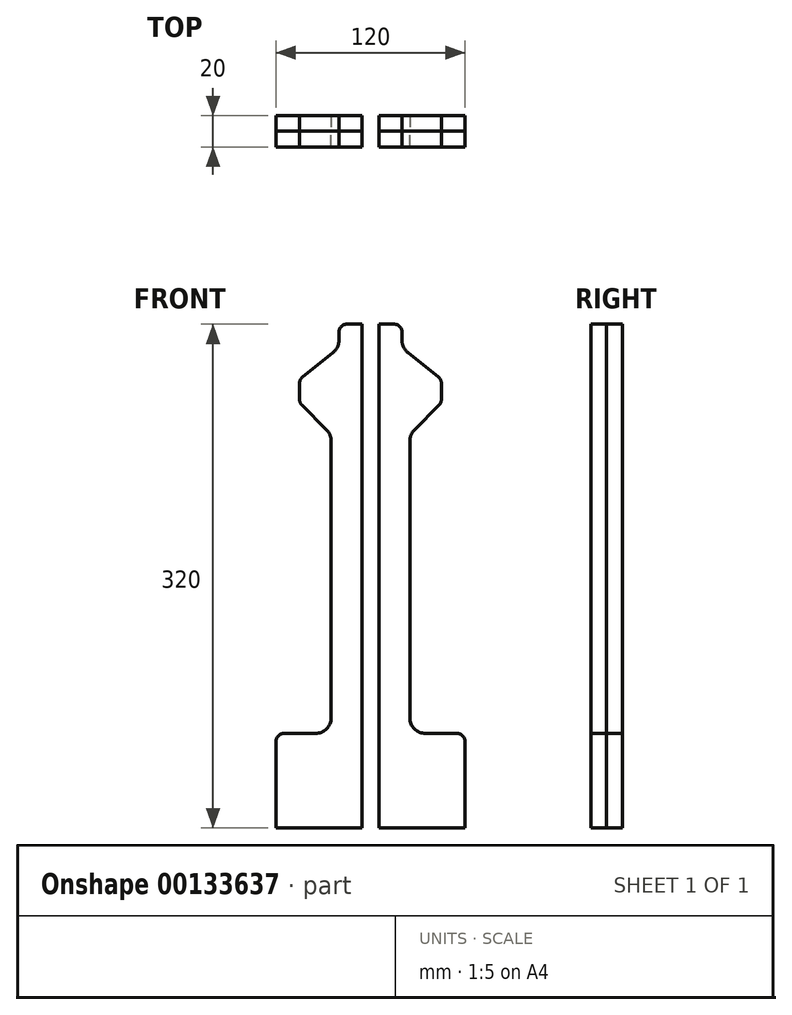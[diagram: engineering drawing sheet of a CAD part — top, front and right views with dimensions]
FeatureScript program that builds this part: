
annotation { "Feature Type Name" : "Feature", "Feature Type Description" : "" }
export const myFeature = defineFeature(function(context is Context, id is Id, definition is map)
    precondition{}
    {
        {
            var Q0;
            Q0=qCreatedBy(makeId("Front.planeOp"),FACE);
            var sketch = newSketch(context, id + "F0", { "sketchPlane" : qUnion([Q0])});
            skLineSegment(sketch, "E0.bottom", {"start": v(55, 30) * mm, "end": v(35, 30) * mm});
            skLineSegment(sketch, "E0.top", {"start": v(60, -30) * mm, "end": v(-60, -30) * mm});
            skLineSegment(sketch, "E0.left", {"start": v(60, 25) * mm, "end": v(60, -30) * mm});
            skLineSegment(sketch, "E0.right", {"start": v(-60, 25) * mm, "end": v(-60, -30) * mm});
            skPoint(sketch, "E0.middle", {"position": v(0, 0) * mm});
            skLineSegment(sketch, "E1", {"start": v(25, 40) * mm, "end": v(25, 215.86) * mm});
            skLineSegment(sketch, "E2", {"start": v(27.93, 222.93) * mm, "end": v(43.54, 238.54) * mm});
            skLineSegment(sketch, "E3", {"start": v(45, 242.07) * mm, "end": v(45, 252.6) * mm});
            skLineSegment(sketch, "E4", {"start": v(43.12, 256.5) * mm, "end": v(23.75, 272) * mm});
            skLineSegment(sketch, "E5", {"start": v(20, 279.8) * mm, "end": v(20, 285) * mm});
            skLineSegment(sketch, "E6", {"start": v(15, 290) * mm, "end": v(-15, 290) * mm});
            skLineSegment(sketch, "E7", {"start": v(-20, 285) * mm, "end": v(-20, 279.8) * mm});
            skLineSegment(sketch, "E8", {"start": v(-23.75, 272) * mm, "end": v(-43.12, 256.5) * mm});
            skLineSegment(sketch, "E9", {"start": v(-45, 252.6) * mm, "end": v(-45, 242.07) * mm});
            skLineSegment(sketch, "E10", {"start": v(-43.54, 238.54) * mm, "end": v(-27.93, 222.93) * mm});
            skLineSegment(sketch, "E11", {"start": v(-25, 215.86) * mm, "end": v(-25, 40) * mm});
            skPoint(sketch, "E12.visualSharp", {"position": v(25, 220) * mm});
            skArc(sketch, "E12.filletArc", {"start": v(27.93, 222.93) * mm, "mid": v(25.76, 219.68) * mm, "end": v(25, 215.86) * mm});
            skPoint(sketch, "E13.visualSharp", {"position": v(-25, 220) * mm});
            skArc(sketch, "E13.filletArc", {"start": v(-25, 215.86) * mm, "mid": v(-25.76, 219.68) * mm, "end": v(-27.93, 222.93) * mm});
            skPoint(sketch, "E14.visualSharp", {"position": v(-20, 275) * mm});
            skArc(sketch, "E14.filletArc", {"start": v(-23.75, 272) * mm, "mid": v(-20.99, 275.47) * mm, "end": v(-20, 279.8) * mm});
            skPoint(sketch, "E15.visualSharp", {"position": v(20, 275) * mm});
            skArc(sketch, "E15.filletArc", {"start": v(20, 279.8) * mm, "mid": v(20.99, 275.47) * mm, "end": v(23.75, 272) * mm});
            skPoint(sketch, "E16.visualSharp", {"position": v(-20, 290) * mm});
            skArc(sketch, "E16.filletArc", {"start": v(-15, 290) * mm, "mid": v(-18.54, 288.54) * mm, "end": v(-20, 285) * mm});
            skPoint(sketch, "E17.visualSharp", {"position": v(20, 290) * mm});
            skArc(sketch, "E17.filletArc", {"start": v(20, 285) * mm, "mid": v(18.54, 288.54) * mm, "end": v(15, 290) * mm});
            skPoint(sketch, "E18.visualSharp", {"position": v(45, 255) * mm});
            skArc(sketch, "E18.filletArc", {"start": v(45, 252.6) * mm, "mid": v(44.5, 254.76) * mm, "end": v(43.12, 256.5) * mm});
            skPoint(sketch, "E19.visualSharp", {"position": v(45, 240) * mm});
            skArc(sketch, "E19.filletArc", {"start": v(43.54, 238.54) * mm, "mid": v(44.62, 240.16) * mm, "end": v(45, 242.07) * mm});
            skPoint(sketch, "E20.visualSharp", {"position": v(-45, 240) * mm});
            skArc(sketch, "E20.filletArc", {"start": v(-45, 242.07) * mm, "mid": v(-44.62, 240.16) * mm, "end": v(-43.54, 238.54) * mm});
            skPoint(sketch, "E21.visualSharp", {"position": v(-45, 255) * mm});
            skArc(sketch, "E21.filletArc", {"start": v(-43.12, 256.5) * mm, "mid": v(-44.5, 254.76) * mm, "end": v(-45, 252.6) * mm});
            skLineSegment(sketch, "E22", {"start": v(-55, 30) * mm, "end": v(-35, 30) * mm});
            skLineSegment(sketch, "E23", {"start": v(25, 30) * mm, "end": v(60, 30) * mm});
            skPoint(sketch, "E24.newPointA", {"position": v(25, 30) * mm});
            skPoint(sketch, "E24.newPointB", {"position": v(-60, 30) * mm});
            skArc(sketch, "E24.filletArc", {"start": v(25, 40) * mm, "mid": v(27.93, 32.93) * mm, "end": v(35, 30) * mm});
            skPoint(sketch, "E25.visualSharp", {"position": v(-25, 30) * mm});
            skArc(sketch, "E25.filletArc", {"start": v(-35, 30) * mm, "mid": v(-27.93, 32.93) * mm, "end": v(-25, 40) * mm});
            skArc(sketch, "E26.filletArc", {"start": v(-55, 30) * mm, "mid": v(-58.54, 28.54) * mm, "end": v(-60, 25) * mm});
            skPoint(sketch, "E27.visualSharp", {"position": v(60, 30) * mm});
            skArc(sketch, "E27.filletArc", {"start": v(60, 25) * mm, "mid": v(58.54, 28.54) * mm, "end": v(55, 30) * mm});
            skLineSegment(sketch, "E28.bottom", {"start": v(-5.5, 290) * mm, "end": v(5.5, 290) * mm});
            skLineSegment(sketch, "E28.top", {"start": v(-5.5, 130) * mm, "end": v(5.5, 130) * mm});
            skLineSegment(sketch, "E28.left", {"start": v(-5.5, 290) * mm, "end": v(-5.5, 130) * mm});
            skLineSegment(sketch, "E28.right", {"start": v(5.5, 290) * mm, "end": v(5.5, 130) * mm});
            skPoint(sketch, "E28.middle", {"position": v(0, 210) * mm});
            skLineSegment(sketch, "E29.bottom", {"start": v(5.5, 130) * mm, "end": v(-5.5, 130) * mm});
            skLineSegment(sketch, "E29.top", {"start": v(5.5, -30) * mm, "end": v(-5.5, -30) * mm});
            skLineSegment(sketch, "E29.left", {"start": v(5.5, 130) * mm, "end": v(5.5, -30) * mm});
            skLineSegment(sketch, "E29.right", {"start": v(-5.5, 130) * mm, "end": v(-5.5, -30) * mm});
            skPoint(sketch, "E29.middle", {"position": v(0, 50) * mm});
            skSolve(sketch);
        }
        {
            var Q0;
            {var subQ3=sQuery(id+"F0.wireOp",EDGE,"E0.right");Q0=makeQuery(id+"F0.imprint","IMPRINT",FACE,{"disambiguationData":[TD([[makeQuery(id+"F0.imprint","IMPRINT",EDGE,{"derivedFrom":subQ3}),1.0]])]});}
            var Q1;
            {var subQ0=sQuery(id+"F0.wireOp",EDGE,"E0.left");Q1=makeQuery(id+"F0.imprint","IMPRINT",FACE,{"disambiguationData":[TD([[makeQuery(id+"F0.imprint","IMPRINT",EDGE,{"derivedFrom":subQ0}),-1.0]])]});}
            var Q2;
            Q2=makeQuery(id+"F0.imprint","IMPRINT",FACE,{"disambiguationData":[TD([[makeQuery(id+"F0.imprint","IMPRINT",EDGE,{"derivedFrom":sQuery(id+"F0.wireOp",EDGE,"E28.bottom")}),-1.0]])]});
            extrude(context, id + "F1", {"entities" : qUnion([Q0, Q1, Q2]), "depth" : 10 * mm});
        }
        {
            var Q0;
            {var subQ3=sQuery(id+"F0.wireOp",EDGE,"E0.right");Q0=makeQuery(id+"F0.imprint","IMPRINT",FACE,{"disambiguationData":[TD([[makeQuery(id+"F0.imprint","IMPRINT",EDGE,{"derivedFrom":subQ3}),1.0]])]});}
            var Q1;
            {var subQ0=sQuery(id+"F0.wireOp",EDGE,"E0.left");Q1=makeQuery(id+"F0.imprint","IMPRINT",FACE,{"disambiguationData":[TD([[makeQuery(id+"F0.imprint","IMPRINT",EDGE,{"derivedFrom":subQ0}),-1.0]])]});}
            var Q2;
            Q2=makeQuery(id+"F0.imprint","IMPRINT",FACE,{"disambiguationData":[TD([[makeQuery(id+"F0.imprint","IMPRINT",EDGE,{"derivedFrom":sQuery(id+"F0.wireOp",EDGE,"E29.bottom")}),1.0]])]});
            extrude(context, id + "F2", {"entities" : qUnion([Q0, Q1, Q2]), "oppositeDirection" : true, "depth" : 10 * mm});
        }
    });
